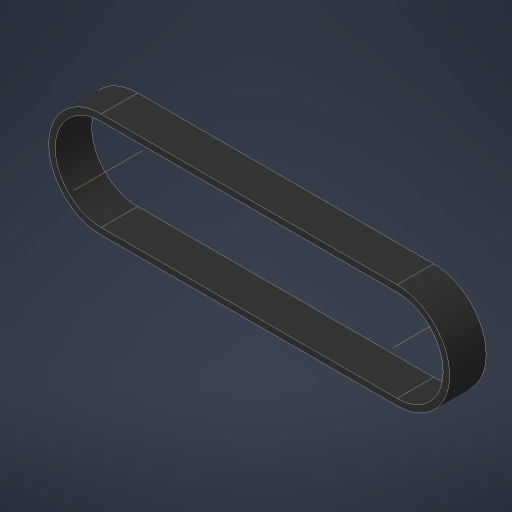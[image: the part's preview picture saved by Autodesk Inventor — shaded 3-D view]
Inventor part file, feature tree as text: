
AUTODESK INVENTOR PART (.ipt)
format: ipt  version: 2023.4 (Build 274418000, 418)  size: 240,128 bytes
history: native  units: in
note: dims shown in document units (in); Inventor stores cm internally (conversion verified against a paired STEP export)
features: sketch x3, extrude x1, other x1, projected_geometry x1
ambient origin geometry x8: Origin, YZ Plane, XZ Plane, XY Plane, X Axis, Y Axis, Z Axis, Center Point
bodies: Body1 (feature_tree)
feature tree (6):
  sketch  "Sketch2"  dims[d0=0.9023in d1=0.9023in]
  extrude  "Extrusion2"  Depth=0.9023in
  sketch  "Sketch5"  dims[d3=1.4174in d5=2.7165in d9=0.0787in d10=0.0598in d11=0.0299in d12=0.0219in d13=0.0219in d14=0.0059in d15=0.0059in d20=0.3346in d21=0.0in d22=0.0787in d23=0.0598in d24=0.0299in d25=0.0219in d26=0.0219in d27=0.0059in d28=0.0059in d29=0.0299in d30=0.0394in d31=0.0787in d32=0.0232in d34=0.0219in d35=0.0in d36=0.0in d37=0.0059in d38=0.0022in d39=0.0022in d40=0.0in d41=0.0in d42=0.0081in d43=0.0081in d44=0.0299in]
  other  "Work Axis1"
  sketch  "Sketch4"  dims[d2=1.4174in]
  projected_geometry  "Projected Loop1"
